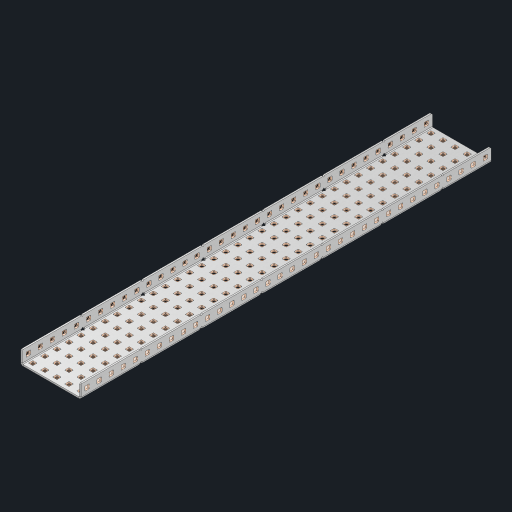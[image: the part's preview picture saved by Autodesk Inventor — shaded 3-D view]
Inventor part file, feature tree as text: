
AUTODESK INVENTOR PART (.ipt)
format: ipt  version: 2023 (Build 270158000, 158)  size: 2,498,048 bytes
history: native  units: in
note: dims shown in document units (in); Inventor stores cm internally (conversion verified against a paired STEP export)
features: other x243, extrude x237, sheet_metal_op x10, sketch x8, mirror x1, pattern_linear x1, chamfer x1
ambient origin geometry x8: Origin, YZ Plane, XZ Plane, XY Plane, X Axis, Y Axis, Z Axis, Center Point
bodies: Solid1 (feature_tree), Body (feature_tree)
feature tree (501):
  other  "Flange Pattern Plane"
  sheet_metal_op  "Flange Pattern"
  sheet_metal_op  "Body Pattern"
  other  "Arc Length"
  mirror  "Notch Mirror"
  pattern_linear  "Notch Pattern"  Spacing1=0.25in  [1 undecoded]
  chamfer  "End Chamfer"
  extrude  "Half Cut"  Depth=0.0625in
  sketch  "Sketch1"  dims[d0=2.5in]
  other  "Plate1"
  sketch  "Sketch2"  dims[d1=17.0in]
  other  "Plate2"
  sheet_metal_op  "Bend1"
  sheet_metal_op  "Corner1"
  sketch  "Sketch3"  dims[d2=0.0625in]
  other  "Flange Pattern Sketch"
  sketch  "Sketch7"  dims[d3=0.0625in]
  other  "Srf1"
  other  "Srf2"
  sketch  "Sketch8"  dims[d4=0.0312in]
  sketch  "Sketch9"  dims[d5=0.125in]
  other  "Srf91"
  sheet_metal_op  "Body Pattern Sketch"
  other  "Srf92"
  sketch  "Sketch13"  dims[d6=0.0625in]
  sketch  "Sketch14"  dims[d7=0.5in d8=90.0deg d9=0.0312in d10=0.25in d11=0.0625in d12=0.0625in d16=0.182in d17=0.02in d18=0.0625in d19=0.0in d20=0.25in d21=0.25in d46=0.172in d47=1.0in d48=0.0in d49=0.182in d50=0.02in d51=0.25in d52=0.25in d53=0.0625in d54=0.0in d55=0.172in d56=1.0in d57=0.0in d60=13.3858in d62=0.5in d63=1.9685in d65=0.5in d85=0.1473in d86=0.1782in d88=0.04in d89=0.0625in d90=0.0in d91=0.04in d92=0.0491in d95=2.5in d96=0.04in d97=0.25in d98=45.0deg d101=0.0in d102=2.497in d131=2.5in d132=13.3858in d134=0.5in d139=0.5in]
  other  "Srf856"
  other  "Srf1310"
  other  "Srf1311"
  other  "Srf1312"
  other  "Srf1376"
  other  "Srf1377"
  other  "Srf1728"
  other  "Srf1755"
  other  "Srf1878"
  other  "Srf1879"
  other  "Srf1880"
  other  "Srf1881"
  other  "Srf1882"
  other  "Srf1883"
  other  "Srf1884"
  other  "Srf1885"
  other  "Srf1886"
  other  "Srf1887"
  other  "Srf1888"
  other  "Srf1889"
  other  "Srf1890"
  other  "Srf1891"
  other  "Srf1892"
  other  "Srf1893"
  other  "Srf1894"
  other  "Srf1895"
  other  "Srf1896"
  other  "Srf1897"
  other  "Srf1898"
  other  "Srf1899"
  other  "Srf1900"
  other  "Srf1901"
  other  "Srf1902"
  other  "Srf1903"
  other  "Srf1904"
  other  "Srf1905"
  other  "Srf1906"
  other  "Srf1942"
  other  "Srf1943"
  other  "Srf1944"
  other  "Srf1945"
  other  "Srf1946"
  other  "Srf1947"
  other  "Srf1948"
  other  "Srf1949"
  other  "Srf1950"
  other  "Srf1951"
  other  "Srf1952"
  other  "Srf1953"
  other  "Srf1954"
  other  "Srf1955"
  other  "Srf1956"
  other  "Srf1957"
  other  "Srf1958"
  other  "Srf1959"
  other  "Srf1960"
  other  "Srf1961"
  other  "Srf1962"
  other  "Srf1963"
  other  "Srf1964"
  other  "Srf1965"
  other  "Srf1966"
  other  "Srf1967"
  other  "Srf1968"
  other  "Srf1969"
  other  "Srf1970"
  other  "Srf2111"
  other  "Srf2112"
  other  "Srf2113"
  other  "Srf2114"
  other  "Srf2115"
  other  "Srf2116"
  other  "Srf2117"
  other  "Srf2118"
  other  "Srf2119"
  other  "Srf2120"
  other  "Srf2121"
  other  "Srf2122"
  other  "Srf2123"
  other  "Srf2124"
  other  "Srf2125"
  other  "Srf2126"
  other  "Srf2127"
  other  "Srf2128"
  other  "Srf2129"
  other  "Srf2130"
  other  "Srf2131"
  other  "Srf2132"
  other  "Srf2133"
  other  "Srf2134"
  other  "Srf2135"
  other  "Srf2136"
  other  "Srf2137"
  other  "Srf2138"
  other  "Srf2139"
  other  "Srf2140"
  other  "Srf2141"
  other  "Srf2142"
  other  "Srf2143"
  other  "Srf2146"
  other  "Srf2147"
  other  "Srf2148"
  other  "Srf2149"
  other  "Srf2150"
  other  "Srf2151"
  other  "Srf2152"
  other  "Srf2153"
  other  "Srf2154"
  other  "Srf2155"
  other  "Srf2156"
  other  "Srf2157"
  other  "Srf2158"
  other  "Srf2159"
  other  "Srf2160"
  other  "Srf2161"
  other  "Srf2162"
  other  "Srf2163"
  other  "Srf2164"
  other  "Srf2165"
  other  "Srf2166"
  other  "Srf2167"
  other  "Srf2168"
  other  "Srf2169"
  other  "Srf2170"
  other  "Srf2171"
  other  "Srf2172"
  other  "Srf2173"
  other  "Srf2174"
  other  "Srf2175"
  other  "Srf2176"
  other  "Srf2177"
  other  "Srf2178"
  other  "Srf2179"
  other  "Srf2180"
  other  "Srf2181"
  other  "Srf2182"
  other  "Srf2183"
  other  "Srf2184"
  other  "Srf2185"
  other  "Srf2186"
  other  "Srf2187"
  other  "Srf2188"
  other  "Srf2189"
  other  "Srf2190"
  other  "Srf2191"
  other  "Srf2192"
  other  "Srf2193"
  other  "Srf2194"
  other  "Srf2195"
  other  "Srf2196"
  other  "Srf2197"
  other  "Srf2198"
  other  "Srf2199"
  other  "Srf2200"
  other  "Srf2201"
  other  "Srf2202"
  other  "Srf2203"
  other  "Srf2204"
  other  "Srf2205"
  other  "Srf2206"
  other  "Srf2207"
  other  "Srf2208"
  other  "Srf2209"
  other  "Srf2210"
  other  "Srf2211"
  other  "Srf2212"
  other  "Srf2213"
  other  "Srf2214"
  other  "Srf2215"
  other  "Srf2216"
  other  "Srf2217"
  other  "Srf2218"
  other  "Srf2219"
  other  "Srf2220"
  other  "Srf2221"
  other  "Srf2222"
  other  "Srf2223"
  other  "Srf2224"
  other  "Srf2225"
  other  "Srf2226"
  other  "Srf2227"
  other  "Srf2228"
  other  "Srf2229"
  other  "Srf2230"
  other  "Srf2231"
  other  "Srf2232"
  other  "Srf2233"
  other  "Srf2234"
  other  "Srf2235"
  other  "Srf2236"
  other  "Srf2237"
  other  "Srf2238"
  other  "Srf2239"
  other  "Srf2240"
  other  "Srf2241"
  other  "Srf2242"
  other  "Srf2243"
  other  "Srf2244"
  other  "Srf2245"
  other  "Srf2246"
  other  "Srf2247"
  other  "Srf2248"
  other  "Srf2249"
  other  "Srf2250"
  other  "Srf2251"
  other  "Srf2252"
  other  "Srf2253"
  other  "Srf2254"
  other  "Srf2255"
  other  "Srf2256"
  other  "Srf2257"
  other  "Srf2258"
  other  "Srf2259"
  other  "Srf2260"
  other  "Srf2261"
  other  "Srf2262"
  other  "Srf2263"
  other  "Srf2264"
  other  "Srf2265"
  other  "Srf2266"
  other  "Srf2267"
  other  "Srf2268"
  other  "Srf2269"
  other  "Srf2270"
  other  "Srf2271"
  other  "Srf2272"
  other  "Srf2273"
  other  "Srf2274"
  other  "Srf2275"
  other  "Srf2276"
  other  "Srf2277"
  other  "Srf2278"
  other  "Srf2279"
  other  "Srf2280"
  sheet_metal_op  "Flange Stamp"
  sheet_metal_op  "Flange Circle"
  sheet_metal_op  "Body Stamp"
  sheet_metal_op  "Body Circle"
  sheet_metal_op  "Notch"
  extrude  "ExtrusionSrf2"  Depth=0.0625in
  extrude  "ExtrusionSrf92"  Depth=2.5in
  extrude  "ExtrusionSrf856"  Depth=0.02in
  extrude  "ExtrusionSrf1310"  Depth=0.0625in
  extrude  "ExtrusionSrf1311"  TaperAngle=0.0deg  [1 undecoded]
  extrude  "ExtrusionSrf1312"  Depth=0.25in
  extrude  "ExtrusionSrf1376"  Depth=0.25in
  extrude  "ExtrusionSrf1377"  Depth=2.5in
  extrude  "ExtrusionSrf1728"  Depth=2.5in TaperAngle=0.0deg
  extrude  "ExtrusionSrf1755"  Depth=2.5in
  extrude  "ExtrusionSrf1878"  Depth=0.02in
  extrude  "ExtrusionSrf1879"  Depth=0.25in
  extrude  "ExtrusionSrf1880"  Depth=0.25in
  extrude  "ExtrusionSrf1881"  Depth=0.0625in
  extrude  "ExtrusionSrf1882"  TaperAngle=0.0deg  [1 undecoded]
  extrude  "ExtrusionSrf1883"  Depth=2.5in
  extrude  "ExtrusionSrf1884"  Depth=2.5in TaperAngle=0.0deg
  extrude  "ExtrusionSrf1885"  Depth=2.5in
  extrude  "ExtrusionSrf1886"  Depth=2.5in
  extrude  "ExtrusionSrf1887"  Depth=2.5in
  extrude  "ExtrusionSrf1888"  Depth=2.5in
  extrude  "ExtrusionSrf1889"  Depth=2.5in
  extrude  "ExtrusionSrf1890"  Depth=0.0625in
  extrude  "ExtrusionSrf1891"  TaperAngle=0.0deg  [1 undecoded]
  extrude  "ExtrusionSrf1892"  Depth=2.5in
  extrude  "ExtrusionSrf1893"  Depth=2.5in
  extrude  "ExtrusionSrf1894"  Depth=2.5in
  extrude  "ExtrusionSrf1895"  Depth=0.25in TaperAngle=45.0deg
  extrude  "ExtrusionSrf1896"  TaperAngle=0.0deg  [1 undecoded]
  extrude  "ExtrusionSrf1897"  Depth=2.5in
  extrude  "ExtrusionSrf1898"  Depth=2.5in
  extrude  "ExtrusionSrf1899"  Depth=2.5in
  extrude  "ExtrusionSrf1900"  Depth=2.5in
  extrude  "ExtrusionSrf1901"  Depth=2.5in
  extrude  "ExtrusionSrf1902"  [1 undecoded]
  extrude  "ExtrusionSrf1903"  [1 undecoded]
  extrude  "ExtrusionSrf1904"  [1 undecoded]
  extrude  "ExtrusionSrf1905"  [1 undecoded]
  extrude  "ExtrusionSrf1906"  [1 undecoded]
  extrude  "ExtrusionSrf1942"  [1 undecoded]
  extrude  "ExtrusionSrf1943"  [1 undecoded]
  extrude  "ExtrusionSrf1944"  [1 undecoded]
  extrude  "ExtrusionSrf1945"  [1 undecoded]
  extrude  "ExtrusionSrf1946"  [1 undecoded]
  extrude  "ExtrusionSrf1947"  [1 undecoded]
  extrude  "ExtrusionSrf1948"  [1 undecoded]
  extrude  "ExtrusionSrf1949"  [1 undecoded]
  extrude  "ExtrusionSrf1950"  [1 undecoded]
  extrude  "ExtrusionSrf1951"  [1 undecoded]
  extrude  "ExtrusionSrf1952"  [1 undecoded]
  extrude  "ExtrusionSrf1953"  [1 undecoded]
  extrude  "ExtrusionSrf1954"  [1 undecoded]
  extrude  "ExtrusionSrf1955"  [1 undecoded]
  extrude  "ExtrusionSrf1956"  [1 undecoded]
  extrude  "ExtrusionSrf1957"  [1 undecoded]
  extrude  "ExtrusionSrf1958"  [1 undecoded]
  extrude  "ExtrusionSrf1959"  [1 undecoded]
  extrude  "ExtrusionSrf1960"  [1 undecoded]
  extrude  "ExtrusionSrf1961"  [1 undecoded]
  extrude  "ExtrusionSrf1962"  [1 undecoded]
  extrude  "ExtrusionSrf1963"  [1 undecoded]
  extrude  "ExtrusionSrf1964"  [1 undecoded]
  extrude  "ExtrusionSrf1965"  [1 undecoded]
  extrude  "ExtrusionSrf1966"  [1 undecoded]
  extrude  "ExtrusionSrf1967"  [1 undecoded]
  extrude  "ExtrusionSrf1968"  [1 undecoded]
  extrude  "ExtrusionSrf1969"  [1 undecoded]
  extrude  "ExtrusionSrf1970"  [1 undecoded]
  extrude  "ExtrusionSrf2111"  [1 undecoded]
  extrude  "ExtrusionSrf2112"  [1 undecoded]
  extrude  "ExtrusionSrf2113"  [1 undecoded]
  extrude  "ExtrusionSrf2114"  [1 undecoded]
  extrude  "ExtrusionSrf2115"  [1 undecoded]
  extrude  "ExtrusionSrf2116"  [1 undecoded]
  extrude  "ExtrusionSrf2117"  [1 undecoded]
  extrude  "ExtrusionSrf2118"  [1 undecoded]
  extrude  "ExtrusionSrf2119"  [1 undecoded]
  extrude  "ExtrusionSrf2120"  [1 undecoded]
  extrude  "ExtrusionSrf2121"  [1 undecoded]
  extrude  "ExtrusionSrf2122"  [1 undecoded]
  extrude  "ExtrusionSrf2123"  [1 undecoded]
  extrude  "ExtrusionSrf2124"  [1 undecoded]
  extrude  "ExtrusionSrf2125"  [1 undecoded]
  extrude  "ExtrusionSrf2126"  [1 undecoded]
  extrude  "ExtrusionSrf2127"  [1 undecoded]
  extrude  "ExtrusionSrf2128"  [1 undecoded]
  extrude  "ExtrusionSrf2129"  [1 undecoded]
  extrude  "ExtrusionSrf2130"  [1 undecoded]
  extrude  "ExtrusionSrf2131"  [1 undecoded]
  extrude  "ExtrusionSrf2132"  [1 undecoded]
  extrude  "ExtrusionSrf2133"  [1 undecoded]
  extrude  "ExtrusionSrf2134"  [1 undecoded]
  extrude  "ExtrusionSrf2135"  [1 undecoded]
  extrude  "ExtrusionSrf2136"  [1 undecoded]
  extrude  "ExtrusionSrf2137"  [1 undecoded]
  extrude  "ExtrusionSrf2138"  [1 undecoded]
  extrude  "ExtrusionSrf2139"  [1 undecoded]
  extrude  "ExtrusionSrf2140"  [1 undecoded]
  extrude  "ExtrusionSrf2141"  [1 undecoded]
  extrude  "ExtrusionSrf2142"  [1 undecoded]
  extrude  "ExtrusionSrf2143"  [1 undecoded]
  extrude  "ExtrusionSrf2146"  [1 undecoded]
  extrude  "ExtrusionSrf2147"  [1 undecoded]
  extrude  "ExtrusionSrf2148"  [1 undecoded]
  extrude  "ExtrusionSrf2149"  [1 undecoded]
  extrude  "ExtrusionSrf2150"  [1 undecoded]
  extrude  "ExtrusionSrf2151"  [1 undecoded]
  extrude  "ExtrusionSrf2152"  [1 undecoded]
  extrude  "ExtrusionSrf2153"  [1 undecoded]
  extrude  "ExtrusionSrf2154"  [1 undecoded]
  extrude  "ExtrusionSrf2155"  [1 undecoded]
  extrude  "ExtrusionSrf2156"  [1 undecoded]
  extrude  "ExtrusionSrf2157"  [1 undecoded]
  extrude  "ExtrusionSrf2158"  [1 undecoded]
  extrude  "ExtrusionSrf2159"  [1 undecoded]
  extrude  "ExtrusionSrf2160"  [1 undecoded]
  extrude  "ExtrusionSrf2161"  [1 undecoded]
  extrude  "ExtrusionSrf2162"  [1 undecoded]
  extrude  "ExtrusionSrf2163"  [1 undecoded]
  extrude  "ExtrusionSrf2164"  [1 undecoded]
  extrude  "ExtrusionSrf2165"  [1 undecoded]
  extrude  "ExtrusionSrf2166"  [1 undecoded]
  extrude  "ExtrusionSrf2167"  [1 undecoded]
  extrude  "ExtrusionSrf2168"  [1 undecoded]
  extrude  "ExtrusionSrf2169"  [1 undecoded]
  extrude  "ExtrusionSrf2170"  [1 undecoded]
  extrude  "ExtrusionSrf2171"  [1 undecoded]
  extrude  "ExtrusionSrf2172"  [1 undecoded]
  extrude  "ExtrusionSrf2173"  [1 undecoded]
  extrude  "ExtrusionSrf2174"  [1 undecoded]
  extrude  "ExtrusionSrf2175"  [1 undecoded]
  extrude  "ExtrusionSrf2176"  [1 undecoded]
  extrude  "ExtrusionSrf2177"  [1 undecoded]
  extrude  "ExtrusionSrf2178"  [1 undecoded]
  extrude  "ExtrusionSrf2179"  [1 undecoded]
  extrude  "ExtrusionSrf2180"  [1 undecoded]
  extrude  "ExtrusionSrf2181"  [1 undecoded]
  extrude  "ExtrusionSrf2182"  [1 undecoded]
  extrude  "ExtrusionSrf2183"  [1 undecoded]
  extrude  "ExtrusionSrf2184"  [1 undecoded]
  extrude  "ExtrusionSrf2185"  [1 undecoded]
  extrude  "ExtrusionSrf2186"  [1 undecoded]
  extrude  "ExtrusionSrf2187"  [1 undecoded]
  extrude  "ExtrusionSrf2188"  [1 undecoded]
  extrude  "ExtrusionSrf2189"  [1 undecoded]
  extrude  "ExtrusionSrf2190"  [1 undecoded]
  extrude  "ExtrusionSrf2191"  [1 undecoded]
  extrude  "ExtrusionSrf2192"  [1 undecoded]
  extrude  "ExtrusionSrf2193"  [1 undecoded]
  extrude  "ExtrusionSrf2194"  [1 undecoded]
  extrude  "ExtrusionSrf2195"  [1 undecoded]
  extrude  "ExtrusionSrf2196"  [1 undecoded]
  extrude  "ExtrusionSrf2197"  [1 undecoded]
  extrude  "ExtrusionSrf2198"  [1 undecoded]
  extrude  "ExtrusionSrf2199"  [1 undecoded]
  extrude  "ExtrusionSrf2200"  [1 undecoded]
  extrude  "ExtrusionSrf2201"  [1 undecoded]
  extrude  "ExtrusionSrf2202"  [1 undecoded]
  extrude  "ExtrusionSrf2203"  [1 undecoded]
  extrude  "ExtrusionSrf2204"  [1 undecoded]
  extrude  "ExtrusionSrf2205"  [1 undecoded]
  extrude  "ExtrusionSrf2206"  [1 undecoded]
  extrude  "ExtrusionSrf2207"  [1 undecoded]
  extrude  "ExtrusionSrf2208"  [1 undecoded]
  extrude  "ExtrusionSrf2209"  [1 undecoded]
  extrude  "ExtrusionSrf2210"  [1 undecoded]
  extrude  "ExtrusionSrf2211"  [1 undecoded]
  extrude  "ExtrusionSrf2212"  [1 undecoded]
  extrude  "ExtrusionSrf2213"  [1 undecoded]
  extrude  "ExtrusionSrf2214"  [1 undecoded]
  extrude  "ExtrusionSrf2215"  [1 undecoded]
  extrude  "ExtrusionSrf2216"  [1 undecoded]
  extrude  "ExtrusionSrf2217"  [1 undecoded]
  extrude  "ExtrusionSrf2218"  [1 undecoded]
  extrude  "ExtrusionSrf2219"  [1 undecoded]
  extrude  "ExtrusionSrf2220"  [1 undecoded]
  extrude  "ExtrusionSrf2221"  [1 undecoded]
  extrude  "ExtrusionSrf2222"  [1 undecoded]
  extrude  "ExtrusionSrf2223"  [1 undecoded]
  extrude  "ExtrusionSrf2224"  [1 undecoded]
  extrude  "ExtrusionSrf2225"  [1 undecoded]
  extrude  "ExtrusionSrf2226"  [1 undecoded]
  extrude  "ExtrusionSrf2227"  [1 undecoded]
  extrude  "ExtrusionSrf2228"  [1 undecoded]
  extrude  "ExtrusionSrf2229"  [1 undecoded]
  extrude  "ExtrusionSrf2230"  [1 undecoded]
  extrude  "ExtrusionSrf2231"  [1 undecoded]
  extrude  "ExtrusionSrf2232"  [1 undecoded]
  extrude  "ExtrusionSrf2233"  [1 undecoded]
  extrude  "ExtrusionSrf2234"  [1 undecoded]
  extrude  "ExtrusionSrf2235"  [1 undecoded]
  extrude  "ExtrusionSrf2236"  [1 undecoded]
  extrude  "ExtrusionSrf2237"  [1 undecoded]
  extrude  "ExtrusionSrf2238"  [1 undecoded]
  extrude  "ExtrusionSrf2239"  [1 undecoded]
  extrude  "ExtrusionSrf2240"  [1 undecoded]
  extrude  "ExtrusionSrf2241"  [1 undecoded]
  extrude  "ExtrusionSrf2242"  [1 undecoded]
  extrude  "ExtrusionSrf2243"  [1 undecoded]
  extrude  "ExtrusionSrf2244"  [1 undecoded]
  extrude  "ExtrusionSrf2245"  [1 undecoded]
  extrude  "ExtrusionSrf2246"  [1 undecoded]
  extrude  "ExtrusionSrf2247"  [1 undecoded]
  extrude  "ExtrusionSrf2248"  [1 undecoded]
  extrude  "ExtrusionSrf2249"  [1 undecoded]
  extrude  "ExtrusionSrf2250"  [1 undecoded]
  extrude  "ExtrusionSrf2251"  [1 undecoded]
  extrude  "ExtrusionSrf2252"  [1 undecoded]
  extrude  "ExtrusionSrf2253"  [1 undecoded]
  extrude  "ExtrusionSrf2254"  [1 undecoded]
  extrude  "ExtrusionSrf2255"  [1 undecoded]
  extrude  "ExtrusionSrf2256"  [1 undecoded]
  extrude  "ExtrusionSrf2257"  [1 undecoded]
  extrude  "ExtrusionSrf2258"  [1 undecoded]
  extrude  "ExtrusionSrf2259"  [1 undecoded]
  extrude  "ExtrusionSrf2260"  [1 undecoded]
  extrude  "ExtrusionSrf2261"  [1 undecoded]
  extrude  "ExtrusionSrf2262"  [1 undecoded]
  extrude  "ExtrusionSrf2263"  [1 undecoded]
  extrude  "ExtrusionSrf2264"  [1 undecoded]
  extrude  "ExtrusionSrf2265"  [1 undecoded]
  extrude  "ExtrusionSrf2266"  [1 undecoded]
  extrude  "ExtrusionSrf2267"  [1 undecoded]
  extrude  "ExtrusionSrf2268"  [1 undecoded]
  extrude  "ExtrusionSrf2269"  [1 undecoded]
  extrude  "ExtrusionSrf2270"  [1 undecoded]
  extrude  "ExtrusionSrf2271"  [1 undecoded]
  extrude  "ExtrusionSrf2272"  [1 undecoded]
  extrude  "ExtrusionSrf2273"  [1 undecoded]
  extrude  "ExtrusionSrf2274"  [1 undecoded]
  extrude  "ExtrusionSrf2275"  [1 undecoded]
  extrude  "ExtrusionSrf2276"  [1 undecoded]
  extrude  "ExtrusionSrf2277"  [1 undecoded]
  extrude  "ExtrusionSrf2278"  [1 undecoded]
  extrude  "ExtrusionSrf2279"  [1 undecoded]
  extrude  "ExtrusionSrf2280"  [1 undecoded]
note: 207 required parameter values undecoded (feature->parameter linkage not recoverable at this tier; creation-order binding heuristic only, values carry confidence <= 0.55)
